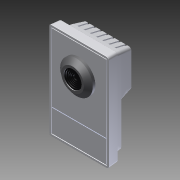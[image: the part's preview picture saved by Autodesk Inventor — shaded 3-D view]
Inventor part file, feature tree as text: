
AUTODESK INVENTOR PART (.ipt)
format: ipt  version: 2014 (Build 180170000, 170)  size: 1,133,568 bytes
history: native  units: in
note: dims shown in document units (in); Inventor stores cm internally (conversion verified against a paired STEP export)
features: fillet x1, other x1, imported_body x1
ambient origin geometry x8: Origin, YZ Plane, XZ Plane, XY Plane, X Axis, Y Axis, Z Axis, Center Point
bodies: Body1 (feature_tree)
feature tree (3):
  fillet  "Fillet18"  [1 undecoded]
  other  "AXIS-M10111"
  imported_body  "Base1"
note: 1 required parameter value undecoded (feature->parameter linkage not recoverable at this tier; creation-order binding heuristic only, values carry confidence <= 0.55)
